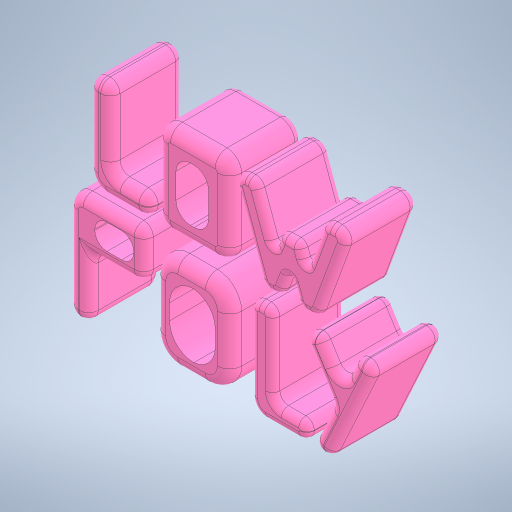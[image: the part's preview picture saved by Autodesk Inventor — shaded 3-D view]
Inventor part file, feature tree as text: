
AUTODESK INVENTOR PART (.ipt)
format: ipt  version: 2024.1 (Build 281209000, 209)  size: 1,051,136 bytes
history: native  units: mm
features: fillet x23, extrude x7, sketch x7, projected_geometry x1
ambient origin geometry x8: Origin, YZ Plane, XZ Plane, XY Plane, X Axis, Y Axis, Z Axis, Center Point
bodies: Solid1 (feature_tree), Solid2 (feature_tree)
feature tree (38):
  extrude  "Extrusion6"  Depth=10.0mm TaperAngle=0.0deg
  extrude  "Extrusion1"  Depth=20.0mm TaperAngle=0.0deg
  extrude  "Extrusion7"  Depth=10.0mm TaperAngle=0.0deg
  fillet  "Fillet1"  Radius=8.2mm
  fillet  "Fillet2"  Radius=10.0mm
  fillet  "Fillet3"  Radius=30.0mm
  fillet  "Fillet4"  Radius=5.5mm
  fillet  "Fillet5"  Radius=5.5mm
  fillet  "Fillet6"  Radius=6.0mm
  fillet  "Fillet7"  Radius=5.8mm
  fillet  "Fillet8"  Radius=36.0mm
  fillet  "Fillet9"  Radius=10.0mm
  fillet  "Fillet10"  Radius=10.0mm
  fillet  "Fillet11"  Radius=160.0mm
  fillet  "Fillet12"  Radius=90.0mm
  fillet  "Fillet13"  Radius=90.0mm
  fillet  "Fillet14"  Radius=19.198622mm
  fillet  "Fillet15"  Radius=19.198622mm
  fillet  "Fillet16"  Radius=10.0mm
  fillet  "Fillet17"  Radius=30.0mm
  fillet  "Fillet18"  [1 undecoded]
  fillet  "Fillet19"  Radius=4.0mm
  fillet  "Fillet20"  Radius=5.0mm
  fillet  "Fillet21"  Radius=5.0mm
  fillet  "Fillet22"  Radius=10.0mm
  fillet  "Fillet23"  Radius=10.0mm
  extrude  "Extrusion2"  Depth=3.5mm
  extrude  "Extrusion3"  Depth=6.0mm
  extrude  "Extrusion4"  Depth=3.5mm
  extrude  "Extrusion5"  Depth=4.0mm
  sketch  "Sketch1"  dims[d0=40.0mm d4=10.0mm d5=0.0mm]
  sketch  "Sketch2"  dims[d6=8.2mm d7=20.0mm d8=0.0mm]
  sketch  "Sketch3"  dims[d9=8.2mm d10=20.0mm d11=0.0mm d12=8.2mm d13=10.0mm d14=0.0mm d15=30.0mm d16=5.5mm d17=5.5mm d18=6.0mm d19=5.8mm d20=36.0mm d21=10.0mm d22=10.0mm d23=0.0mm d24=160.0mm d25=90.0mm d26=90.0mm d27=0.0mm d28=19.198622mm d29=19.198622mm d31=10.0mm d39=30.0mm d40=0.0mm d41=0.0mm d42=4.0mm d43=5.0mm d44=5.0mm d45=10.0mm d46=10.0mm]
  sketch  "Sketch4"  dims[d47=5.0mm d48=3.5mm]
  sketch  "Sketch5"  dims[d49=3.0mm d50=6.0mm]
  sketch  "Sketch6"  dims[d51=3.5mm d52=3.5mm]
  projected_geometry  "Projected Loop1"
  sketch  "Sketch7"  dims[d53=4.0mm d54=4.0mm d55=7.0mm d56=6.0mm d57=6.0mm d58=5.0mm d59=4.0mm d60=1.0mm d61=3.0mm d62=3.0mm d63=19.198622mm d64=7.056118mm d65=7.5mm d66=6.0mm d67=3.0mm d69=3.931055mm d70=3.9mm]
note: 1 required parameter value undecoded (feature->parameter linkage not recoverable at this tier; creation-order binding heuristic only, values carry confidence <= 0.55)
